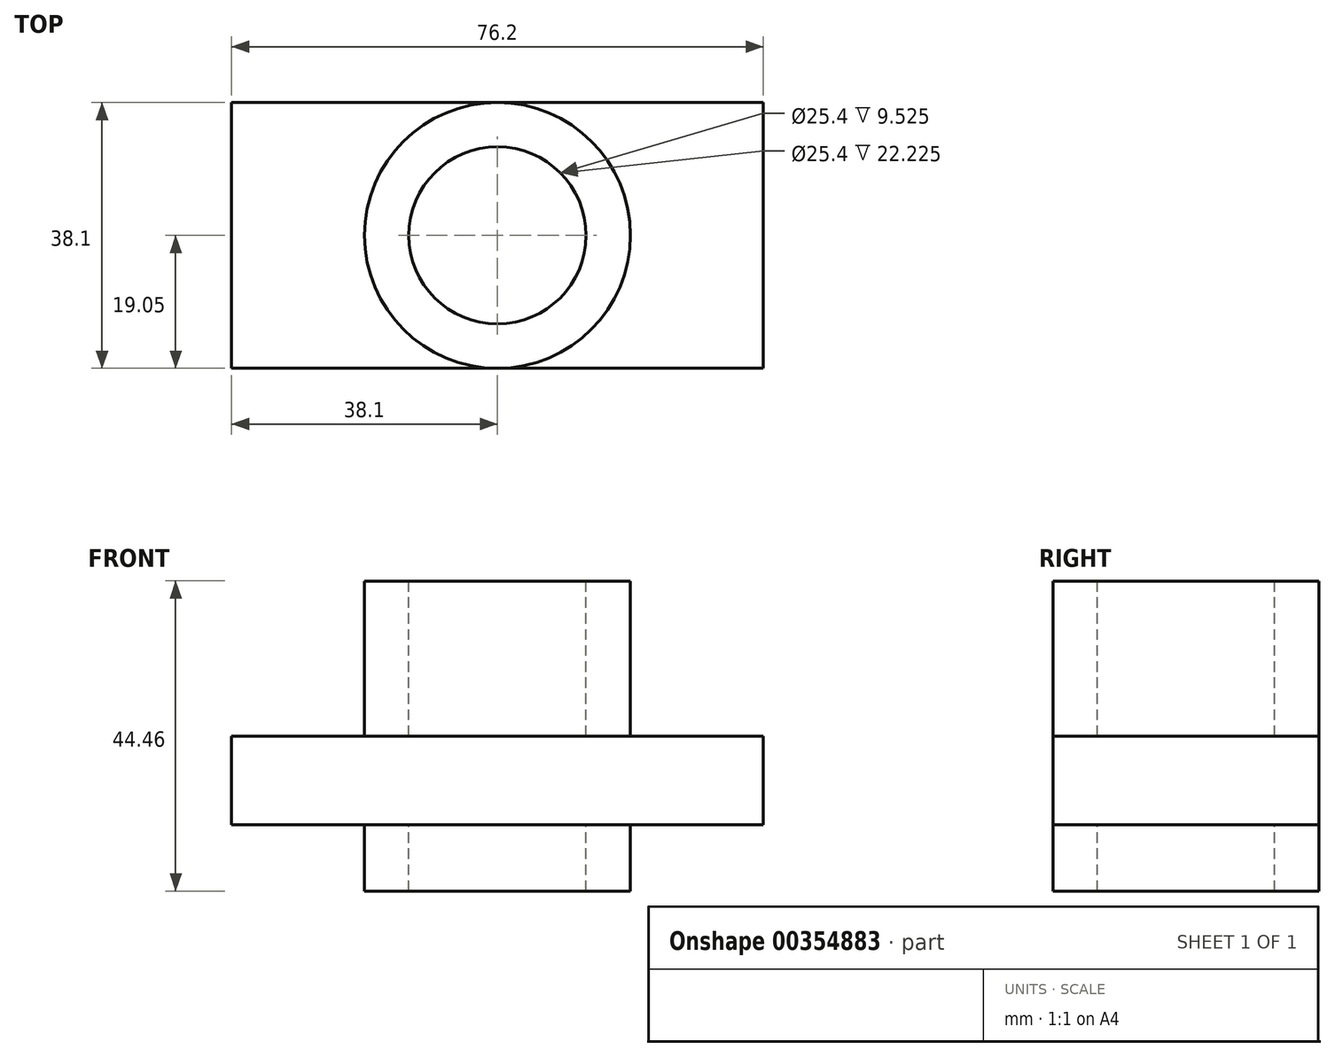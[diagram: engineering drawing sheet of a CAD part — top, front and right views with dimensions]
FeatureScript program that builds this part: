
annotation { "Feature Type Name" : "Feature", "Feature Type Description" : "" }
export const myFeature = defineFeature(function(context is Context, id is Id, definition is map)
    precondition{}
    {
        {
            var Q0;
            Q0=qCreatedBy(makeId("Top.planeOp"),FACE);
            var sketch = newSketch(context, id + "F0", { "sketchPlane" : qUnion([Q0])});
            skLineSegment(sketch, "E0.bottom", {"start": v(0, 0) * mm, "end": v(76.2, 0) * mm});
            skLineSegment(sketch, "E0.top", {"start": v(0, 38.1) * mm, "end": v(76.2, 38.1) * mm});
            skLineSegment(sketch, "E0.left", {"start": v(0, 0) * mm, "end": v(0, 38.1) * mm});
            skLineSegment(sketch, "E0.right", {"start": v(76.2, 0) * mm, "end": v(76.2, 38.1) * mm});
            skSolve(sketch);
        }
        {
            var Q0;
            Q0 = qSketchRegion(id + "F0", true);
            extrude(context, id + "F1", {"entities" : qUnion([Q0]), "depth" : 12.7 * mm});
        }
        {
            var Q0;
            Q0=makeQuery(id+"F1.opExtrude","CAP_FACE",FACE,{"disambiguationData":[OSD([sQuery(id+"F0.wireOp",EDGE,"E0.bottom"),sQuery(id+"F0.wireOp",EDGE,"E0.top"),sQuery(id+"F0.wireOp",EDGE,"E0.left"),sQuery(id+"F0.wireOp",EDGE,"E0.right")])],"isStart":false});
            var sketch = newSketch(context, id + "F2", { "sketchPlane" : qUnion([Q0])});
            skCircle(sketch, "E1", {"center": v(38.1, 19.05) * mm, "radius": 9.53 * mm});
            skPoint(sketch, "E2", {"position": v(38.1, 38.1) * mm});
            skPoint(sketch, "E3", {"position": v(0, 19.05) * mm});
            skCircle(sketch, "E4", {"center": v(38.1, 19.05) * mm, "radius": 19.05 * mm});
            skCircle(sketch, "E5", {"center": v(38.1, 19.05) * mm, "radius": 12.7 * mm});
            skSolve(sketch);
        }
        {
            var Q0;
            Q0 = qSketchRegion(id + "F2", true);
            extrude(context, id + "F3", {"entities" : qUnion([Q0]), "operationType" : NewBodyOperationType.ADD, "endBound" : BoundingType.SYMMETRIC, "oppositeDirection" : true, "depth" : 44.45 * mm});
        }
    });
